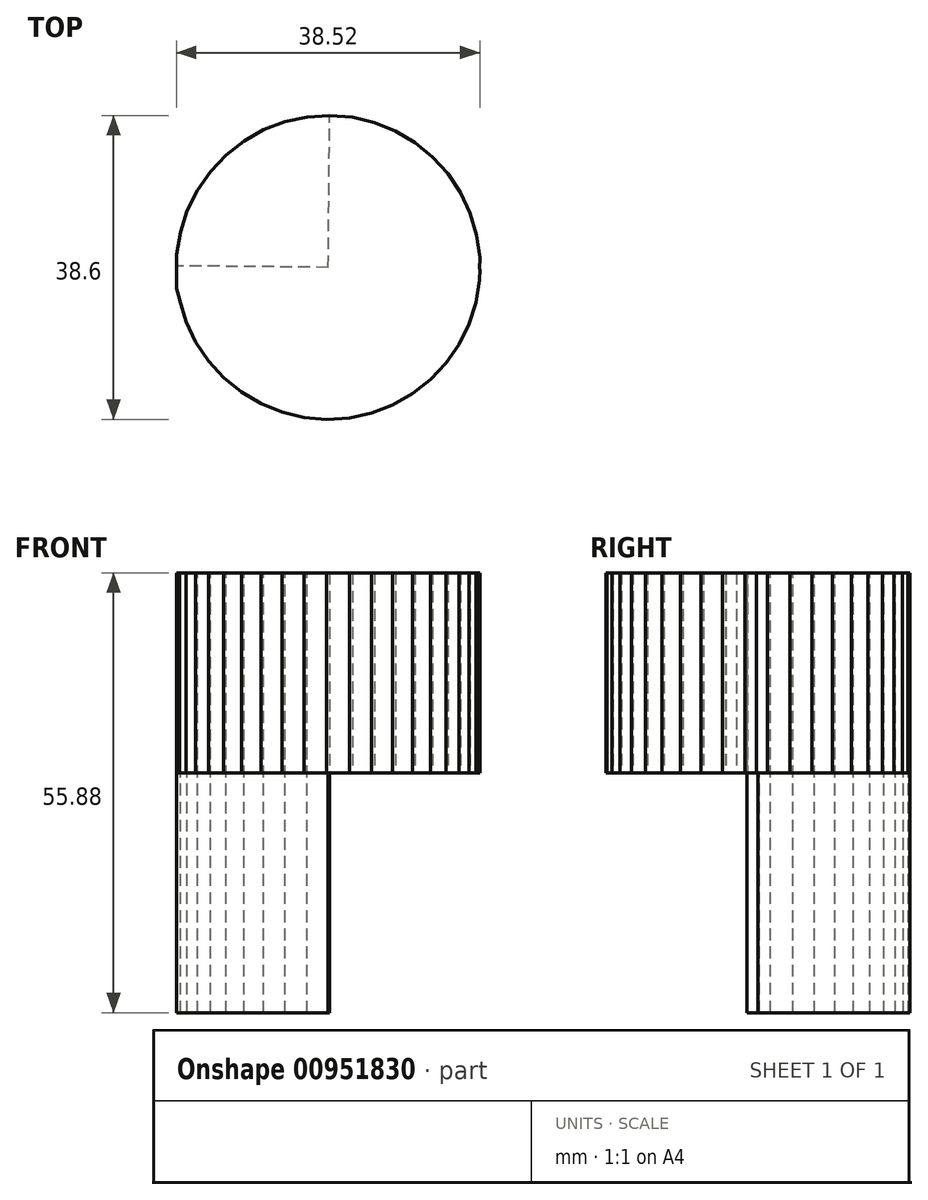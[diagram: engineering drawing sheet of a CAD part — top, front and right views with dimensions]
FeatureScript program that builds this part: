
annotation { "Feature Type Name" : "Feature", "Feature Type Description" : "" }
export const myFeature = defineFeature(function(context is Context, id is Id, definition is map)
    precondition{}
    {
        {
            var Q0;
            Q0=qCreatedBy(makeId("Top.planeOp"),FACE);
            var sketch = newSketch(context, id + "F0", { "sketchPlane" : qUnion([Q0])});
            skCircle(sketch, "E0.cCircle", {"center": v(0, 0) * mm, "radius": 19.25 * mm, "construction": true});
            skLineSegment(sketch, "E0.0", {"start": v(-17.9, 7.23) * mm, "end": v(-16.62, 9.82) * mm});
            skLineSegment(sketch, "E0.1", {"start": v(-16.62, 9.82) * mm, "end": v(-14.97, 12.19) * mm});
            skLineSegment(sketch, "E0.2", {"start": v(-14.97, 12.19) * mm, "end": v(-12.99, 14.28) * mm});
            skLineSegment(sketch, "E0.3", {"start": v(-12.99, 14.28) * mm, "end": v(-10.71, 16.06) * mm});
            skLineSegment(sketch, "E0.4", {"start": v(-10.71, 16.06) * mm, "end": v(-8.2, 17.48) * mm});
            skLineSegment(sketch, "E0.5", {"start": v(-8.2, 17.48) * mm, "end": v(-5.5, 18.5) * mm});
            skLineSegment(sketch, "E0.6", {"start": v(-5.5, 18.5) * mm, "end": v(-2.69, 19.12) * mm});
            skLineSegment(sketch, "E0.7", {"start": v(-2.69, 19.12) * mm, "end": v(0.2, 19.3) * mm});
            skLineSegment(sketch, "E0.8", {"start": v(0.2, 19.3) * mm, "end": v(3.07, 19.06) * mm});
            skLineSegment(sketch, "E0.9", {"start": v(3.07, 19.06) * mm, "end": v(5.87, 18.39) * mm});
            skLineSegment(sketch, "E0.10", {"start": v(5.87, 18.39) * mm, "end": v(8.55, 17.3) * mm});
            skLineSegment(sketch, "E0.11", {"start": v(8.55, 17.3) * mm, "end": v(11.03, 15.84) * mm});
            skLineSegment(sketch, "E0.12", {"start": v(11.03, 15.84) * mm, "end": v(13.27, 14.02) * mm});
            skLineSegment(sketch, "E0.13", {"start": v(13.27, 14.02) * mm, "end": v(15.21, 11.88) * mm});
            skLineSegment(sketch, "E0.14", {"start": v(15.21, 11.88) * mm, "end": v(16.81, 9.48) * mm});
            skLineSegment(sketch, "E0.15", {"start": v(16.81, 9.48) * mm, "end": v(18.04, 6.87) * mm});
            skLineSegment(sketch, "E0.16", {"start": v(18.04, 6.87) * mm, "end": v(18.86, 4.1) * mm});
            skLineSegment(sketch, "E0.17", {"start": v(18.86, 4.1) * mm, "end": v(19.26, 1.25) * mm});
            skLineSegment(sketch, "E0.18", {"start": v(19.26, 1.25) * mm, "end": v(19.24, -1.63) * mm});
            skLineSegment(sketch, "E0.19", {"start": v(19.24, -1.63) * mm, "end": v(18.78, -4.48) * mm});
            skLineSegment(sketch, "E0.20", {"start": v(18.78, -4.48) * mm, "end": v(17.9, -7.23) * mm});
            skLineSegment(sketch, "E0.21", {"start": v(17.9, -7.23) * mm, "end": v(16.62, -9.82) * mm});
            skLineSegment(sketch, "E0.22", {"start": v(16.62, -9.82) * mm, "end": v(14.97, -12.19) * mm});
            skLineSegment(sketch, "E0.23", {"start": v(14.97, -12.19) * mm, "end": v(12.99, -14.28) * mm});
            skLineSegment(sketch, "E0.24", {"start": v(12.99, -14.28) * mm, "end": v(10.71, -16.06) * mm});
            skLineSegment(sketch, "E0.25", {"start": v(10.71, -16.06) * mm, "end": v(8.2, -17.48) * mm});
            skLineSegment(sketch, "E0.26", {"start": v(8.2, -17.48) * mm, "end": v(5.5, -18.5) * mm});
            skLineSegment(sketch, "E0.27", {"start": v(5.5, -18.5) * mm, "end": v(2.69, -19.12) * mm});
            skLineSegment(sketch, "E0.28", {"start": v(2.69, -19.12) * mm, "end": v(-0.2, -19.3) * mm});
            skLineSegment(sketch, "E0.29", {"start": v(-0.2, -19.3) * mm, "end": v(-3.07, -19.06) * mm});
            skLineSegment(sketch, "E0.30", {"start": v(-3.07, -19.06) * mm, "end": v(-5.87, -18.39) * mm});
            skLineSegment(sketch, "E0.31", {"start": v(-5.87, -18.39) * mm, "end": v(-8.55, -17.3) * mm});
            skLineSegment(sketch, "E0.32", {"start": v(-8.55, -17.3) * mm, "end": v(-11.03, -15.84) * mm});
            skLineSegment(sketch, "E0.33", {"start": v(-11.03, -15.84) * mm, "end": v(-13.27, -14.02) * mm});
            skLineSegment(sketch, "E0.34", {"start": v(-13.27, -14.02) * mm, "end": v(-15.21, -11.88) * mm});
            skLineSegment(sketch, "E0.35", {"start": v(-15.21, -11.88) * mm, "end": v(-16.81, -9.48) * mm});
            skLineSegment(sketch, "E0.36", {"start": v(-16.81, -9.48) * mm, "end": v(-18.04, -6.87) * mm});
            skLineSegment(sketch, "E0.37", {"start": v(-18.04, -6.87) * mm, "end": v(-18.86, -4.1) * mm});
            skLineSegment(sketch, "E0.38", {"start": v(-18.86, -4.1) * mm, "end": v(-19.26, -1.25) * mm});
            skLineSegment(sketch, "E0.39", {"start": v(-19.26, -1.25) * mm, "end": v(-19.24, 1.63) * mm});
            skLineSegment(sketch, "E0.40", {"start": v(-19.24, 1.63) * mm, "end": v(-18.78, 4.48) * mm});
            skLineSegment(sketch, "E0.41", {"start": v(-18.78, 4.48) * mm, "end": v(-17.9, 7.23) * mm});
            skPoint(sketch, "E0.0.midPoint", {"position": v(-17.26, 8.53) * mm});
            skLineSegment(sketch, "E1", {"start": v(0, 0) * mm, "end": v(0.2, 19.3) * mm});
            skLineSegment(sketch, "E2", {"start": v(0, 0) * mm, "end": v(19.26, -0.2) * mm});
            skLineSegment(sketch, "E3", {"start": v(19.26, -0.2) * mm, "end": v(19.24, -1.63) * mm});
            skLineSegment(sketch, "E4", {"start": v(0, 0) * mm, "end": v(-0.2, -19.3) * mm});
            skLineSegment(sketch, "E5", {"start": v(0, 0) * mm, "end": v(-19.24, 0.2) * mm});
            skLineSegment(sketch, "E6", {"start": v(-19.24, 0.2) * mm, "end": v(-19.26, -2.7) * mm});
            skLineSegment(sketch, "E7", {"start": v(-19.26, -2.7) * mm, "end": v(-18.04, -6.87) * mm});
            skSolve(sketch);
        }
        {
            var Q0;
            Q0=makeQuery(id+"F0.imprint","IMPRINT",FACE,{"disambiguationData":[TD([[makeQuery(id+"F0.imprint","IMPRINT",EDGE,{"derivedFrom":sQuery(id+"F0.wireOp",EDGE,"E0.0")}),-1.0]])]});
            extrude(context, id + "F1", {"entities" : qUnion([Q0]), "oppositeDirection" : true, "depth" : 30.48 * mm, "offsetDistance" : 25.4 * mm});
        }
        {
            var Q0;
            Q0 = qSketchRegion(id + "F0", true);
            extrude(context, id + "F2", {"entities" : qUnion([Q0]), "operationType" : NewBodyOperationType.ADD, "depth" : 25.4 * mm, "offsetDistance" : 25.4 * mm});
        }
    });
